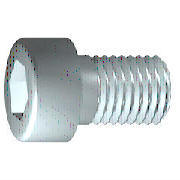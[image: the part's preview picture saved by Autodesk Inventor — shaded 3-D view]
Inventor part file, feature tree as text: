
AUTODESK INVENTOR PART (.ipt)
format: ipt  version: 2018 (Build 220112000, 112)  size: 184,832 bytes
history: native  units: mm (DEFAULTED — no unit token found)
features: sketch x2, extrude x1, plane x1, fillet x1
ambient origin geometry x7: Origin, YZ Plane, XY Plane, X Axis, Y Axis, Z Axis, Center Point
bodies: Solid1 (feature_tree), Body (feature_tree)
feature tree (5):
  extrude  "Slot"  Depth=4.0mm
  plane  "Work Plane1"
  fillet  "Fillet2"  Radius=4.0mm
  sketch  "Sketch1"  dims[d1=20.0mm d2=0.429515mm d3=4.0mm]
  sketch  "Sketch2"  dims[d4=2.0mm d5=60.0deg d6=4.0mm d7=4.0mm d8=3.464102mm d9=7.0mm d10=90.0deg d11=10.0mm d12=0.0mm d13=20.0mm d14=0.0mm d15=0.429415mm d16=0.429415mm d17=0.4mm d19=0.0mm d26=30.0mm d27=45.0deg d28=0.0mm d29=0.0mm d30=0.1mm]
